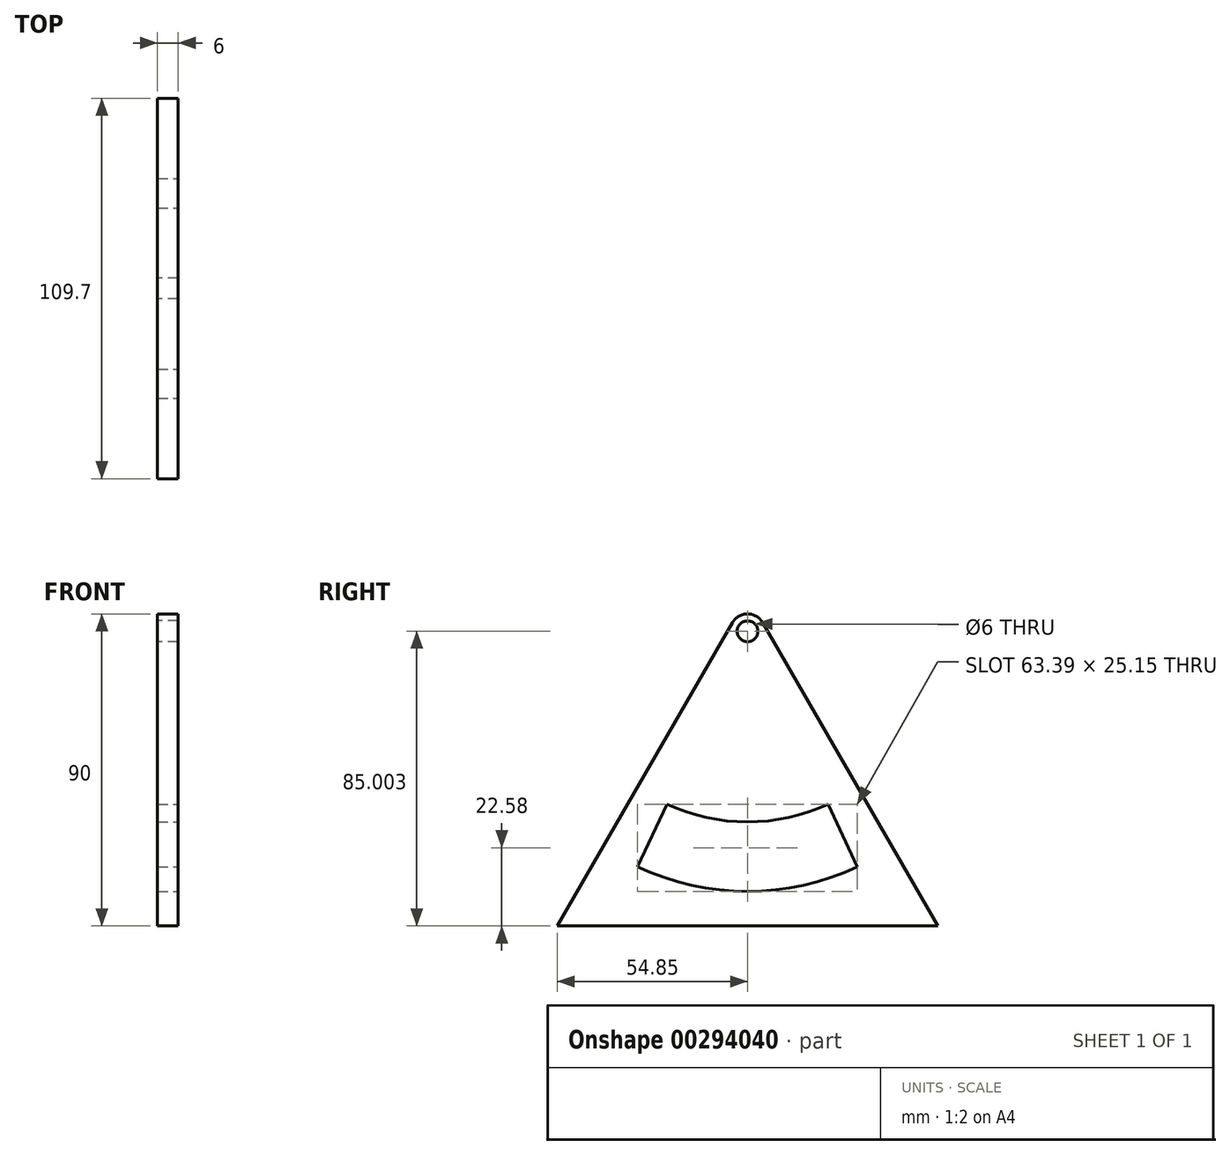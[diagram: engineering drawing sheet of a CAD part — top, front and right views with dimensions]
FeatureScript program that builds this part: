
annotation { "Feature Type Name" : "Feature", "Feature Type Description" : "" }
export const myFeature = defineFeature(function(context is Context, id is Id, definition is map)
    precondition{}
    {
        {
            var Q0;
            Q0=qCreatedBy(makeId("Right.planeOp"),FACE);
            var sketch = newSketch(context, id + "F0", { "sketchPlane" : qUnion([Q0])});
            skCircle(sketch, "E0.cCircle", {"center": v(0, 0) * mm, "radius": 63.33 * mm, "construction": true});
            skLineSegment(sketch, "E0.0", {"start": v(-54.85, -31.67) * mm, "end": v(0, 63.33) * mm});
            skLineSegment(sketch, "E0.1", {"start": v(0, 63.33) * mm, "end": v(54.85, -31.67) * mm});
            skLineSegment(sketch, "E0.2", {"start": v(54.85, -31.67) * mm, "end": v(-54.85, -31.67) * mm});
            skLineSegment(sketch, "E1", {"start": v(0, 63.33) * mm, "end": v(0, -31.67) * mm, "construction": true});
            skCircle(sketch, "E2", {"center": v(0, 53.33) * mm, "radius": 3 * mm});
            skSolve(sketch);
        }
        {
            var Q0;
            Q0 = qSketchRegion(id + "F0", true);
            extrude(context, id + "F1", {"entities" : qUnion([Q0]), "depth" : 6 * mm, "offsetDistance" : 25 * mm});
        }
        {
            var Q0;
            Q0=makeQuery(id+"F1.opExtrude","CAP_FACE",FACE,{"disambiguationData":[OSD([sQuery(id+"F0.wireOp",EDGE,"E0.0"),sQuery(id+"F0.wireOp",EDGE,"E0.1"),sQuery(id+"F0.wireOp",EDGE,"E0.2"),sQuery(id+"F0.wireOp",EDGE,"E2")])],"isStart":false});
            var sketch = newSketch(context, id + "F2", { "sketchPlane" : qUnion([Q0])});
            skArc(sketch, "E3", {"start": v(-23.24, 3.49) * mm, "mid": v(0, -1.67) * mm, "end": v(23.24, 3.49) * mm});
            skLineSegment(sketch, "E4", {"start": v(0, 53.33) * mm, "end": v(0, -31.67) * mm, "construction": true});
            skLineSegment(sketch, "E5", {"start": v(0, 53.33) * mm, "end": v(-23.24, 3.49) * mm});
            skLineSegment(sketch, "E6", {"start": v(0, 53.33) * mm, "end": v(23.24, 3.49) * mm});
            skArc(sketch, "E7.0", {"start": v(-31.7, -14.64) * mm, "mid": v(0, -21.67) * mm, "end": v(31.7, -14.64) * mm});
            skLineSegment(sketch, "E8", {"start": v(-23.24, 3.49) * mm, "end": v(-31.7, -14.64) * mm});
            skLineSegment(sketch, "E9", {"start": v(23.24, 3.49) * mm, "end": v(31.7, -14.64) * mm});
            skSolve(sketch);
        }
        {
            var Q0;
            Q0=makeQuery(id+"F2.imprint","IMPRINT",FACE,{"disambiguationData":[TD([[makeQuery(id+"F2.imprint","IMPRINT",EDGE,{"derivedFrom":sQuery(id+"F2.wireOp",EDGE,"E3")}),-1.0]])]});
            extrude(context, id + "F3", {"entities" : qUnion([Q0]), "operationType" : NewBodyOperationType.REMOVE, "endBound" : BoundingType.UP_TO_NEXT, "oppositeDirection" : true, "depth" : 25 * mm, "offsetDistance" : 25 * mm});
        }
        {
            var Q0;
            Q0=makeQuery(id+"F1.opExtrude","SWEPT_EDGE",EDGE,{"disambiguationData":[OSD([sQuery(id+"F0.wireOp",EDGE,"E0.0"),sQuery(id+"F0.wireOp",EDGE,"E0.1")])]});
            fillet(context, id + "F4", {"entities" : qUnion([Q0]), "tangentPropagation" : true, "radius" : 5 * mm, "defaultsChanged" : false, "vertexSettings" : [], "allowEdgeOverflow" : false});
        }
    });
